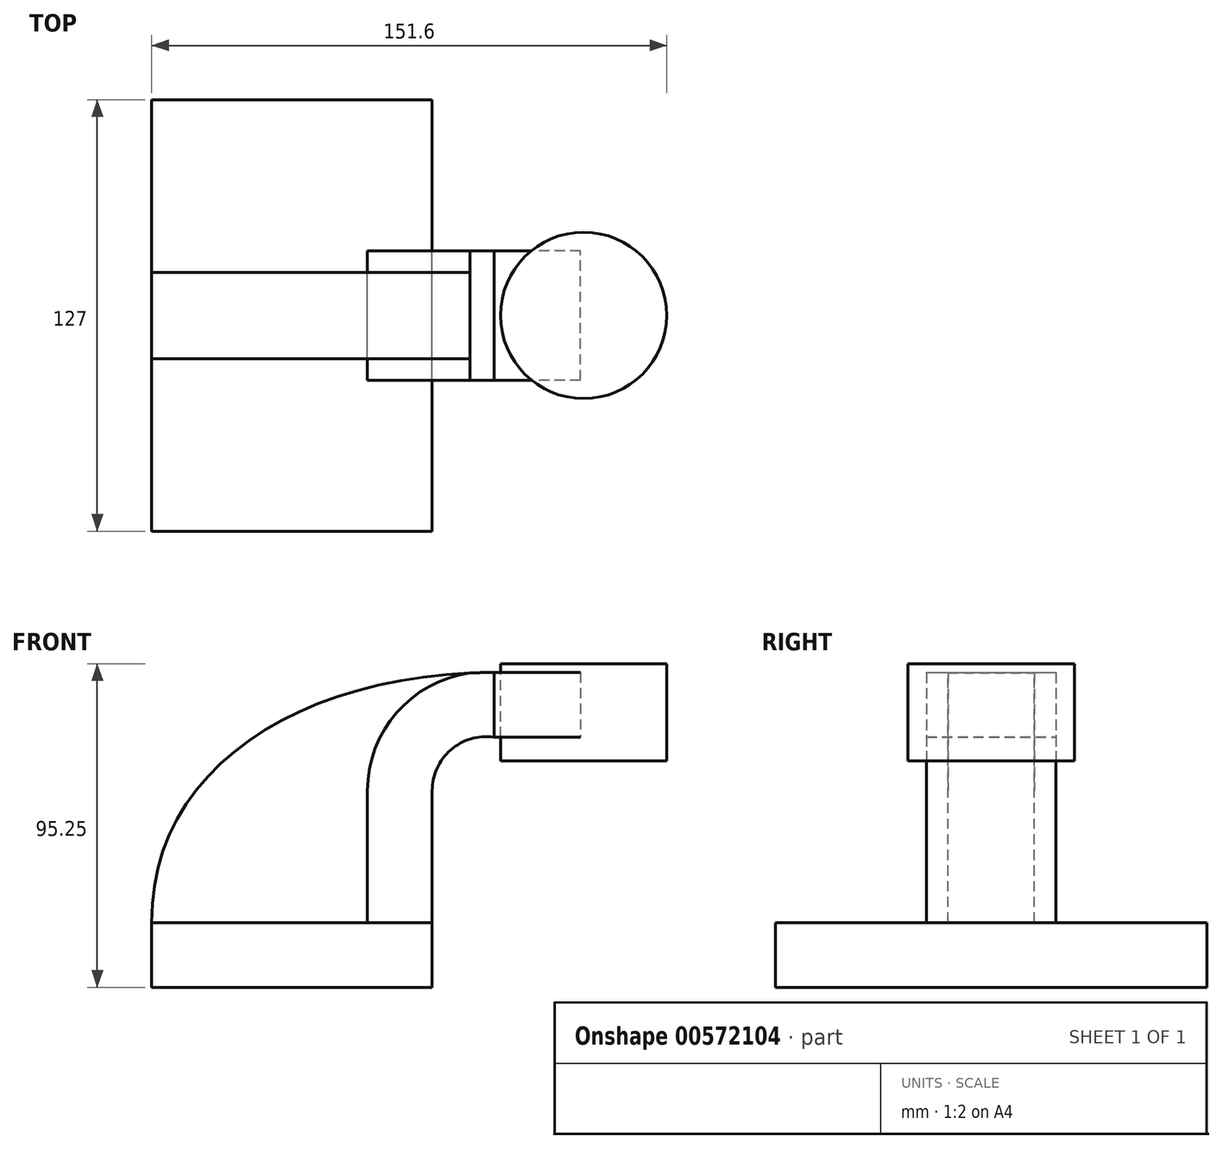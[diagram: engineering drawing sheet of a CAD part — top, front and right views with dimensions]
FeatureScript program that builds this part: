
annotation { "Feature Type Name" : "Feature", "Feature Type Description" : "" }
export const myFeature = defineFeature(function(context is Context, id is Id, definition is map)
    precondition{}
    {
        {
            var Q0;
            Q0=qCreatedBy(makeId("Front.planeOp"),FACE);
            var sketch = newSketch(context, id + "F0", { "sketchPlane" : qUnion([Q0])});
            skLineSegment(sketch, "E0.bottom", {"start": v(62.32, -1.8) * mm, "end": v(-20.23, -1.8) * mm});
            skLineSegment(sketch, "E0.top", {"start": v(62.32, -20.86) * mm, "end": v(-20.23, -20.86) * mm});
            skLineSegment(sketch, "E0.left", {"start": v(62.32, -1.8) * mm, "end": v(62.32, -20.86) * mm});
            skLineSegment(sketch, "E0.right", {"start": v(-20.23, -1.8) * mm, "end": v(-20.23, -20.86) * mm});
            skLineSegment(sketch, "E1", {"start": v(62.32, -1.8) * mm, "end": v(62.32, 37.03) * mm});
            skLineSegment(sketch, "E2.bottom", {"start": v(80.56, 74.4) * mm, "end": v(131.36, 74.4) * mm});
            skLineSegment(sketch, "E2.top", {"start": v(80.56, 45.82) * mm, "end": v(131.36, 45.82) * mm});
            skLineSegment(sketch, "E2.left", {"start": v(131.36, 74.4) * mm, "end": v(131.36, 45.82) * mm});
            skLineSegment(sketch, "E2.right", {"start": v(80.56, 74.4) * mm, "end": v(80.56, 45.82) * mm});
            skLineSegment(sketch, "E3", {"start": v(80.36, 52.76) * mm, "end": v(105.75, 52.76) * mm});
            skArc(sketch, "E4", {"start": v(80.36, 52.76) * mm, "mid": v(67.76, 49) * mm, "end": v(62.32, 37.03) * mm});
            skPoint(sketch, "E5", {"position": v(106.77, 60.1) * mm});
            skLineSegment(sketch, "E6.0", {"start": v(81.41, 71.81) * mm, "end": v(106.9, 71.81) * mm});
            skArc(sketch, "E6.1", {"start": v(81.41, 71.81) * mm, "mid": v(54.66, 62.84) * mm, "end": v(43.27, 37.03) * mm});
            skLineSegment(sketch, "E6.2", {"start": v(43.27, -1.8) * mm, "end": v(43.27, 37.03) * mm});
            skFitSpline(sketch, "E7", {"points": [v(-20.23, -1.8) * mm, v(81.41, 71.81) * mm], "startDerivative": vector(-1.5, 135.77) * mm, "endDerivative": vector(173.6, -0.08) * mm});
            skLineSegment(sketch, "E8", {"start": v(106.9, 74.4) * mm, "end": v(106.9, 45.82) * mm});
            skSolve(sketch);
        }
        {
            var Q0;
            Q0=makeQuery(id+"F0.imprint","IMPRINT",FACE,{"disambiguationData":[TD([[makeQuery(id+"F0.imprint","IMPRINT",EDGE,{"derivedFrom":sQuery(id+"F0.wireOp",EDGE,"E0.top")}),-1.0]])]});
            extrude(context, id + "F1", {"entities" : qUnion([Q0]), "endBound" : BoundingType.SYMMETRIC, "depth" : 127 * mm, "offsetDistance" : 25.4 * mm});
        }
        {
            var Q0;
            {var subQ1=sQuery(id+"F0.wireOp",EDGE,"E2.bottom");Q0=makeQuery(id+"F0.imprint","IMPRINT",FACE,{"disambiguationData":[TD([[makeQuery(id+"F0.imprint","IMPRINT",EDGE,{"derivedFrom":subQ1}),-1.0]])]});}
            extrude(context, id + "F2", {"entities" : qUnion([Q0]), "operationType" : NewBodyOperationType.REMOVE, "endBound" : BoundingType.SYMMETRIC, "depth" : 76.2 * mm, "offsetDistance" : 25.4 * mm});
        }
        {
            var Q0;
            {var subQ0=sQuery(id+"F0.wireOp",EDGE,"E4");Q0=makeQuery(id+"F0.imprint","IMPRINT",FACE,{"disambiguationData":[TD([[makeQuery(id+"F0.imprint","IMPRINT",EDGE,{"derivedFrom":subQ0}),-1.0]])]});}
            extrude(context, id + "F3", {"entities" : qUnion([Q0]), "endBound" : BoundingType.SYMMETRIC, "depth" : 38.1 * mm, "offsetDistance" : 25.4 * mm});
        }
        {
            var Q0;
            {var subQ3=sQuery(id+"F0.wireOp",EDGE,"E6.2");Q0=makeQuery(id+"F0.imprint","IMPRINT",FACE,{"disambiguationData":[TD([[makeQuery(id+"F0.imprint","IMPRINT",EDGE,{"derivedFrom":subQ3}),1.0]])]});}
            extrude(context, id + "F4", {"entities" : qUnion([Q0]), "endBound" : BoundingType.SYMMETRIC, "depth" : 25.4 * mm, "offsetDistance" : 25.4 * mm});
        }
        {
            var Q0;
            {var subQ4=sQuery(id+"F0.wireOp",EDGE,"E2.left");Q0=makeQuery(id+"F0.imprint","IMPRINT",FACE,{"disambiguationData":[TD([[makeQuery(id+"F0.imprint","IMPRINT",EDGE,{"derivedFrom":subQ4}),-1.0]])]});}
            var Q1;
            Q1=sQuery(id+"F0.wireOp",EDGE,"E8");
            revolve(context, id + "F5", {"entities" : qUnion([Q0]), "axis" : qUnion([Q1]), "revolveType" : RevolveType.FULL});
        }
        {
            var Q0;
            Q0=makeQuery(id+"F3.opExtrude","SWEPT_FACE",FACE,{"disambiguationData":[OSD([sQuery(id+"F0.wireOp",EDGE,"E2.right")])]});
            extrude(context, id + "F6", {"entities" : qUnion([Q0]), "depth" : 25.4 * mm, "offsetDistance" : 25.4 * mm});
        }
    });
